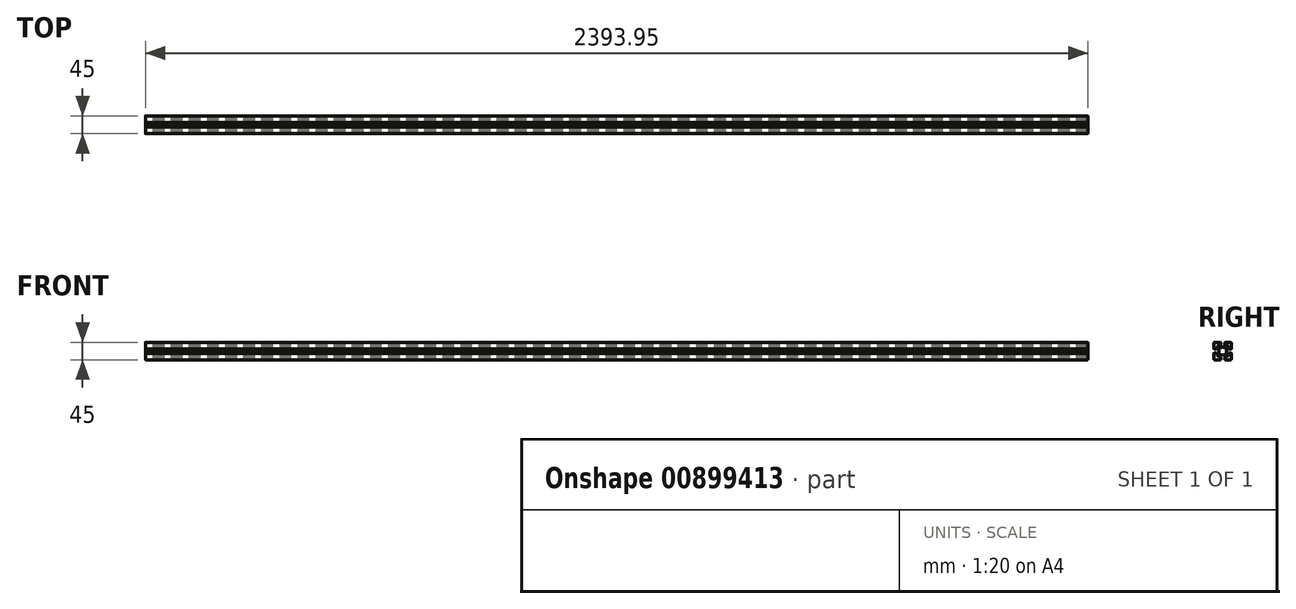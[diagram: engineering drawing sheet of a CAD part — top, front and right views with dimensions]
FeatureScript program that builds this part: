
annotation { "Feature Type Name" : "Feature", "Feature Type Description" : "" }
export const myFeature = defineFeature(function(context is Context, id is Id, definition is map)
    precondition{}
    {
        {
            var Q0;
            Q0=qCreatedBy(makeId("Right.planeOp"),FACE);
            var sketch = newSketch(context, id + "F0", { "sketchPlane" : qUnion([Q0])});
            skLineSegment(sketch, "E0", {"start": v(-20.09, -10.29) * mm, "end": v(-21.29, -10.29) * mm});
            skArc(sketch, "E1", {"start": v(-21.29, -10.29) * mm, "mid": v(-21.5, -10.38) * mm, "end": v(-21.59, -10.59) * mm});
            skLineSegment(sketch, "E2", {"start": v(-21.59, -10.59) * mm, "end": v(-21.59, -23.99) * mm});
            skArc(sketch, "E3", {"start": v(-21.59, -23.99) * mm, "mid": v(-20.7, -26.11) * mm, "end": v(-18.59, -26.99) * mm});
            skLineSegment(sketch, "E4", {"start": v(-18.59, -26.99) * mm, "end": v(-5.19, -26.99) * mm});
            skArc(sketch, "E5", {"start": v(-5.19, -26.99) * mm, "mid": v(-4.98, -26.9) * mm, "end": v(-4.89, -26.69) * mm});
            skLineSegment(sketch, "E6", {"start": v(-4.89, -26.69) * mm, "end": v(-4.89, -25.49) * mm});
            skLineSegment(sketch, "E7", {"start": v(-4.89, -25.49) * mm, "end": v(-4.39, -25.49) * mm});
            skArc(sketch, "E8", {"start": v(-4.39, -25.49) * mm, "mid": v(-4.18, -25.4) * mm, "end": v(-4.09, -25.19) * mm});
            skLineSegment(sketch, "E9", {"start": v(-4.09, -25.19) * mm, "end": v(-4.09, -21.29) * mm});
            skArc(sketch, "E10", {"start": v(-4.09, -21.29) * mm, "mid": v(-4.18, -21.08) * mm, "end": v(-4.39, -20.99) * mm});
            skLineSegment(sketch, "E11", {"start": v(-4.39, -20.99) * mm, "end": v(-9.14, -20.99) * mm});
            skLineSegment(sketch, "E12", {"start": v(-9.14, -20.99) * mm, "end": v(-9.14, -16.88) * mm});
            skLineSegment(sketch, "E13", {"start": v(-9.14, -16.88) * mm, "end": v(-6.25, -13.99) * mm});
            skLineSegment(sketch, "E14", {"start": v(-6.25, -13.99) * mm, "end": v(-2.21, -13.99) * mm});
            skArc(sketch, "E15", {"start": v(-2.21, -13.99) * mm, "mid": v(0.91, -14.49) * mm, "end": v(4.03, -13.99) * mm});
            skLineSegment(sketch, "E16", {"start": v(-20.09, -10.29) * mm, "end": v(-20.09, -9.79) * mm});
            skArc(sketch, "E17", {"start": v(-20.09, -9.79) * mm, "mid": v(-20, -9.58) * mm, "end": v(-19.79, -9.49) * mm});
            skLineSegment(sketch, "E18", {"start": v(-19.79, -9.49) * mm, "end": v(-15.89, -9.49) * mm});
            skArc(sketch, "E19", {"start": v(-15.89, -9.49) * mm, "mid": v(-15.68, -9.58) * mm, "end": v(-15.59, -9.79) * mm});
            skLineSegment(sketch, "E20", {"start": v(-15.59, -9.79) * mm, "end": v(-15.59, -14.54) * mm});
            skLineSegment(sketch, "E21", {"start": v(-15.59, -14.54) * mm, "end": v(-11.48, -14.54) * mm});
            skLineSegment(sketch, "E22", {"start": v(-11.48, -14.54) * mm, "end": v(-8.59, -11.65) * mm});
            skLineSegment(sketch, "E23", {"start": v(-8.59, -11.65) * mm, "end": v(-8.59, -7.61) * mm});
            skLineSegment(sketch, "E24", {"start": v(29.82, -4.49) * mm, "end": v(-31.05, -4.49) * mm});
            skLineSegment(sketch, "E25.MirrorCS", {"start": v(6.71, -25.49) * mm, "end": v(6.21, -25.49) * mm});
            skArc(sketch, "E26.MirrorCS", {"start": v(7.01, -26.99) * mm, "mid": v(6.8, -26.9) * mm, "end": v(6.71, -26.69) * mm});
            skLineSegment(sketch, "E27.MirrorCS", {"start": v(10.41, -11.65) * mm, "end": v(10.41, -7.61) * mm});
            skArc(sketch, "E28.MirrorCS", {"start": v(6.21, -25.49) * mm, "mid": v(6, -25.4) * mm, "end": v(5.91, -25.19) * mm});
            skLineSegment(sketch, "E29.MirrorCS", {"start": v(6.71, -26.69) * mm, "end": v(6.71, -25.49) * mm});
            skArc(sketch, "E30.MirrorCS", {"start": v(5.91, -21.29) * mm, "mid": v(6, -21.08) * mm, "end": v(6.21, -20.99) * mm});
            skLineSegment(sketch, "E31.MirrorCS", {"start": v(10.96, -16.88) * mm, "end": v(8.07, -13.99) * mm});
            skLineSegment(sketch, "E32.MirrorCS", {"start": v(13.3, -14.54) * mm, "end": v(10.41, -11.65) * mm});
            skLineSegment(sketch, "E33.MirrorCS", {"start": v(17.41, -14.54) * mm, "end": v(13.3, -14.54) * mm});
            skLineSegment(sketch, "E34.MirrorCS", {"start": v(17.41, -9.79) * mm, "end": v(17.41, -14.54) * mm});
            skLineSegment(sketch, "E35.MirrorCS", {"start": v(6.21, -20.99) * mm, "end": v(10.96, -20.99) * mm});
            skLineSegment(sketch, "E36.MirrorCS", {"start": v(8.07, -13.99) * mm, "end": v(4.03, -13.99) * mm});
            skArc(sketch, "E37.MirrorCS", {"start": v(4.03, -13.99) * mm, "mid": v(0.91, -14.49) * mm, "end": v(-2.21, -13.99) * mm});
            skLineSegment(sketch, "E38.MirrorCS", {"start": v(10.96, -20.99) * mm, "end": v(10.96, -16.88) * mm});
            skLineSegment(sketch, "E39.MirrorCS", {"start": v(5.91, -25.19) * mm, "end": v(5.91, -21.29) * mm});
            skArc(sketch, "E40.MirrorCS", {"start": v(23.41, -23.99) * mm, "mid": v(22.53, -26.11) * mm, "end": v(20.41, -26.99) * mm});
            skLineSegment(sketch, "E41.MirrorCS", {"start": v(20.41, -26.99) * mm, "end": v(7.01, -26.99) * mm});
            skLineSegment(sketch, "E42.MirrorCS", {"start": v(23.41, -10.59) * mm, "end": v(23.41, -23.99) * mm});
            skArc(sketch, "E43.MirrorCS", {"start": v(17.71, -9.49) * mm, "mid": v(17.5, -9.58) * mm, "end": v(17.41, -9.79) * mm});
            skArc(sketch, "E44.MirrorCS", {"start": v(23.11, -10.29) * mm, "mid": v(23.32, -10.38) * mm, "end": v(23.41, -10.59) * mm});
            skLineSegment(sketch, "E45.MirrorCS", {"start": v(21.91, -10.29) * mm, "end": v(21.91, -9.79) * mm});
            skLineSegment(sketch, "E46.MirrorCS", {"start": v(21.91, -10.29) * mm, "end": v(23.11, -10.29) * mm});
            skArc(sketch, "E47.MirrorCS", {"start": v(21.91, -9.79) * mm, "mid": v(21.82, -9.58) * mm, "end": v(21.61, -9.49) * mm});
            skLineSegment(sketch, "E48.MirrorCS", {"start": v(21.61, -9.49) * mm, "end": v(17.71, -9.49) * mm});
            skLineSegment(sketch, "E49.MirrorCS", {"start": v(6.71, 16.51) * mm, "end": v(6.21, 16.51) * mm});
            skArc(sketch, "E50.MirrorCS", {"start": v(-4.39, 16.51) * mm, "mid": v(-4.18, 16.42) * mm, "end": v(-4.09, 16.21) * mm});
            skLineSegment(sketch, "E51.MirrorCS", {"start": v(-4.89, 16.51) * mm, "end": v(-4.39, 16.51) * mm});
            skArc(sketch, "E52.MirrorCS", {"start": v(5.91, 12.31) * mm, "mid": v(6, 12.1) * mm, "end": v(6.21, 12.01) * mm});
            skLineSegment(sketch, "E53.MirrorCS", {"start": v(6.71, 17.71) * mm, "end": v(6.71, 16.51) * mm});
            skLineSegment(sketch, "E54.MirrorCS", {"start": v(-4.89, 17.71) * mm, "end": v(-4.89, 16.51) * mm});
            skArc(sketch, "E55.MirrorCS", {"start": v(-5.19, 18.01) * mm, "mid": v(-4.98, 17.92) * mm, "end": v(-4.89, 17.71) * mm});
            skArc(sketch, "E56.MirrorCS", {"start": v(-4.09, 12.31) * mm, "mid": v(-4.18, 12.1) * mm, "end": v(-4.39, 12.01) * mm});
            skArc(sketch, "E57.MirrorCS", {"start": v(7.01, 18.01) * mm, "mid": v(6.8, 17.92) * mm, "end": v(6.71, 17.71) * mm});
            skArc(sketch, "E58.MirrorCS", {"start": v(6.21, 16.51) * mm, "mid": v(6, 16.42) * mm, "end": v(5.91, 16.21) * mm});
            skArc(sketch, "E59.MirrorCS", {"start": v(23.11, 1.31) * mm, "mid": v(23.32, 1.4) * mm, "end": v(23.41, 1.61) * mm});
            skLineSegment(sketch, "E60.MirrorCS", {"start": v(21.91, 1.31) * mm, "end": v(21.91, 0.81) * mm});
            skArc(sketch, "E61.MirrorCS", {"start": v(-15.89, 0.51) * mm, "mid": v(-15.68, 0.6) * mm, "end": v(-15.59, 0.81) * mm});
            skArc(sketch, "E62.MirrorCS", {"start": v(-21.29, 1.31) * mm, "mid": v(-21.5, 1.4) * mm, "end": v(-21.59, 1.61) * mm});
            skArc(sketch, "E63.MirrorCS", {"start": v(17.71, 0.51) * mm, "mid": v(17.5, 0.6) * mm, "end": v(17.41, 0.81) * mm});
            skArc(sketch, "E64.MirrorCS", {"start": v(21.91, 0.81) * mm, "mid": v(21.82, 0.6) * mm, "end": v(21.61, 0.51) * mm});
            skLineSegment(sketch, "E65.MirrorCS", {"start": v(21.91, 1.31) * mm, "end": v(23.11, 1.31) * mm});
            skArc(sketch, "E66.MirrorCS", {"start": v(14.31, 5.31) * mm, "mid": v(14.1, 5.4) * mm, "end": v(14.01, 5.61) * mm});
            skArc(sketch, "E67.MirrorCS", {"start": v(-20.09, 0.81) * mm, "mid": v(-20, 0.6) * mm, "end": v(-19.79, 0.51) * mm});
            skLineSegment(sketch, "E68.MirrorCS", {"start": v(-20.09, 1.31) * mm, "end": v(-21.29, 1.31) * mm});
            skLineSegment(sketch, "E69.MirrorCS", {"start": v(-20.09, 1.31) * mm, "end": v(-20.09, 0.81) * mm});
            skLineSegment(sketch, "E70.MirrorCS", {"start": v(8.07, 5.01) * mm, "end": v(4.03, 5.01) * mm});
            skLineSegment(sketch, "E71.MirrorCS", {"start": v(-4.09, 16.21) * mm, "end": v(-4.09, 12.31) * mm});
            skLineSegment(sketch, "E72.MirrorCS", {"start": v(-9.14, 12.01) * mm, "end": v(-9.14, 7.9) * mm});
            skLineSegment(sketch, "E73.MirrorCS", {"start": v(-15.59, 5.56) * mm, "end": v(-11.48, 5.56) * mm});
            skLineSegment(sketch, "E74.MirrorCS", {"start": v(-4.39, 12.01) * mm, "end": v(-9.14, 12.01) * mm});
            skLineSegment(sketch, "E75.MirrorCS", {"start": v(-9.14, 7.9) * mm, "end": v(-6.25, 5.01) * mm});
            skLineSegment(sketch, "E76.MirrorCS", {"start": v(10.96, 12.01) * mm, "end": v(10.96, 7.9) * mm});
            skArc(sketch, "E77.MirrorCS", {"start": v(-21.59, 15.01) * mm, "mid": v(-20.7, 17.13) * mm, "end": v(-18.59, 18.01) * mm});
            skLineSegment(sketch, "E78.MirrorCS", {"start": v(23.41, 1.61) * mm, "end": v(23.41, 15.01) * mm});
            skLineSegment(sketch, "E79.MirrorCS", {"start": v(13.3, 5.56) * mm, "end": v(10.41, 2.67) * mm});
            skLineSegment(sketch, "E80.MirrorCS", {"start": v(-8.59, 2.67) * mm, "end": v(-8.59, -1.37) * mm});
            skLineSegment(sketch, "E81.MirrorCS", {"start": v(-15.59, 0.81) * mm, "end": v(-15.59, 5.56) * mm});
            skLineSegment(sketch, "E82.MirrorCS", {"start": v(10.41, 2.67) * mm, "end": v(10.41, -1.37) * mm});
            skLineSegment(sketch, "E83.MirrorCS", {"start": v(-18.59, 18.01) * mm, "end": v(-5.19, 18.01) * mm});
            skLineSegment(sketch, "E84.MirrorCS", {"start": v(10.96, 7.9) * mm, "end": v(8.07, 5.01) * mm});
            skLineSegment(sketch, "E85.MirrorCS", {"start": v(17.41, 5.56) * mm, "end": v(13.3, 5.56) * mm});
            skArc(sketch, "E86.MirrorCS", {"start": v(23.41, 15.01) * mm, "mid": v(22.53, 17.13) * mm, "end": v(20.41, 18.01) * mm});
            skLineSegment(sketch, "E87.MirrorCS", {"start": v(5.91, 16.21) * mm, "end": v(5.91, 12.31) * mm});
            skLineSegment(sketch, "E88.MirrorCS", {"start": v(17.41, 0.81) * mm, "end": v(17.41, 5.56) * mm});
            skLineSegment(sketch, "E89.MirrorCS", {"start": v(-11.48, 5.56) * mm, "end": v(-8.59, 2.67) * mm});
            skLineSegment(sketch, "E90.MirrorCS", {"start": v(-6.25, 5.01) * mm, "end": v(-2.21, 5.01) * mm});
            skLineSegment(sketch, "E91.MirrorCS", {"start": v(-21.59, 1.61) * mm, "end": v(-21.59, 15.01) * mm});
            skArc(sketch, "E92.MirrorCS", {"start": v(4.03, 5.01) * mm, "mid": v(0.91, 5.51) * mm, "end": v(-2.21, 5.01) * mm});
            skLineSegment(sketch, "E93.MirrorCS", {"start": v(6.21, 12.01) * mm, "end": v(10.96, 12.01) * mm});
            skArc(sketch, "E94.MirrorCS", {"start": v(-2.21, 5.01) * mm, "mid": v(0.91, 5.51) * mm, "end": v(4.03, 5.01) * mm});
            skLineSegment(sketch, "E95.MirrorCS", {"start": v(20.41, 18.01) * mm, "end": v(7.01, 18.01) * mm});
            skLineSegment(sketch, "E96.MirrorCS", {"start": v(-19.79, 0.51) * mm, "end": v(-15.89, 0.51) * mm});
            skLineSegment(sketch, "E97.MirrorCS", {"start": v(21.61, 0.51) * mm, "end": v(17.71, 0.51) * mm});
            skLineSegment(sketch, "E98.MirrorCS", {"start": v(0.91, -27.65) * mm, "end": v(0.91, 19.82) * mm});
            skArc(sketch, "E99", {"start": v(-8.59, -1.37) * mm, "mid": v(-9.09, -4.49) * mm, "end": v(-8.59, -7.61) * mm});
            skArc(sketch, "E100", {"start": v(10.41, -7.61) * mm, "mid": v(10.91, -4.49) * mm, "end": v(10.41, -1.37) * mm});
            skSolve(sketch);
        }
        {
            var Q0;
            Q0=qSketchRegion(id+"F0",true);
            extrude(context, id + "F1", {"entities" : qUnion([Q0]), "depth" : 2393.95 * mm, "offsetDistance" : 25.4 * mm});
        }
    });
